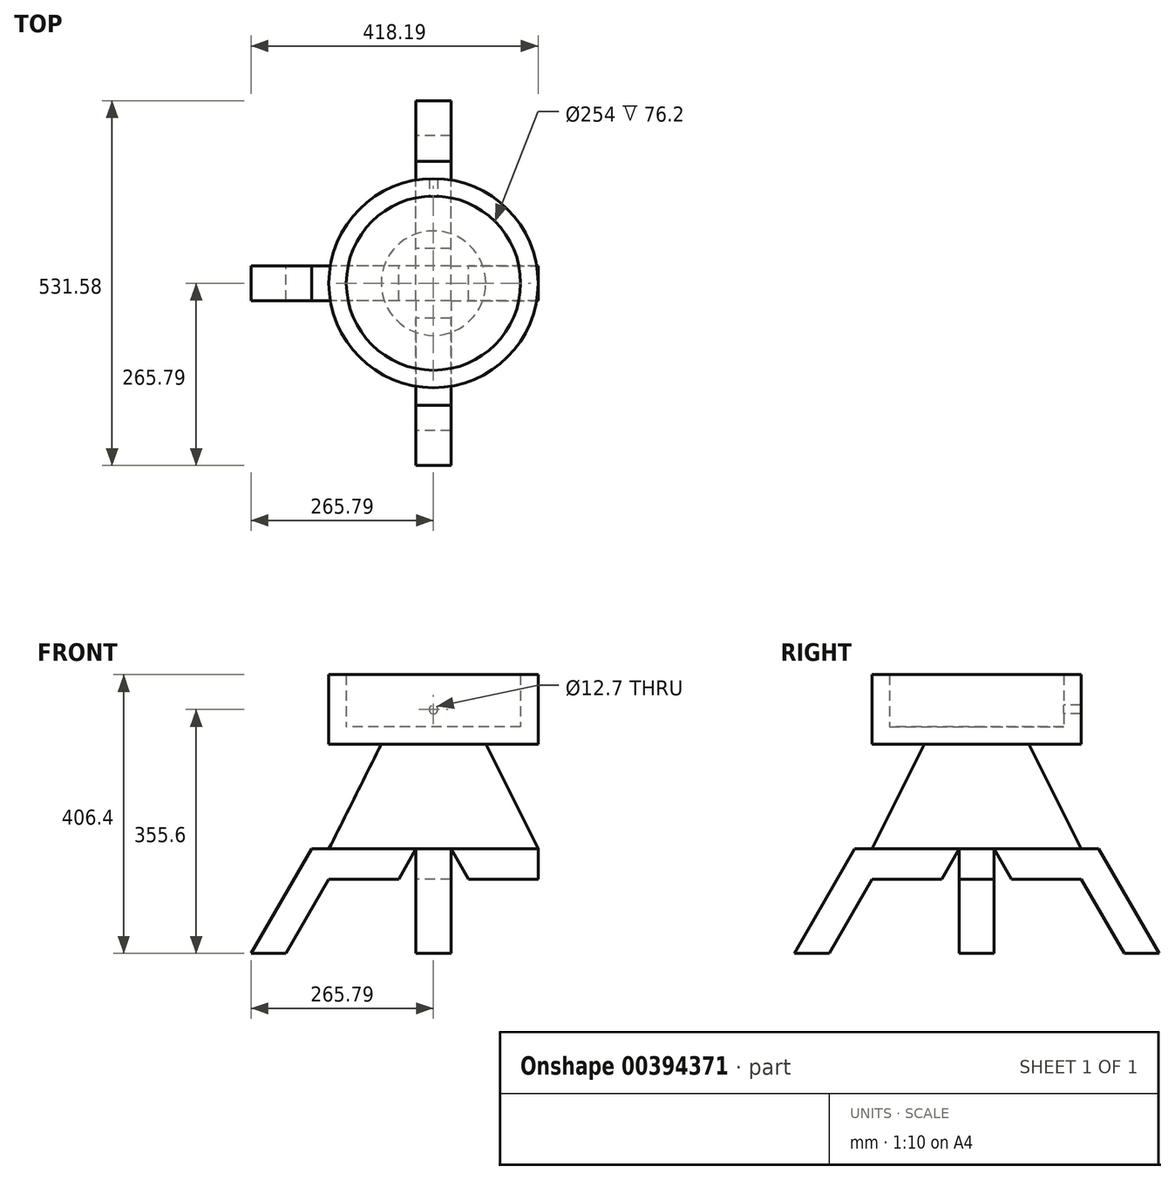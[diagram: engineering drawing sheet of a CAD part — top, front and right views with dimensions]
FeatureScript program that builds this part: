
annotation { "Feature Type Name" : "Feature", "Feature Type Description" : "" }
export const myFeature = defineFeature(function(context is Context, id is Id, definition is map)
    precondition{}
    {
        {
            var Q0;
            Q0=qCreatedBy(makeId("Top.planeOp"),FACE);
            var sketch = newSketch(context, id + "F0", { "sketchPlane" : qUnion([Q0])});
            skCircle(sketch, "E0", {"center": v(0, 0) * mm, "radius": 152.4 * mm});
            skCircle(sketch, "E1", {"center": v(0, 0) * mm, "radius": 127 * mm});
            skSolve(sketch);
        }
        {
            var Q0;
            Q0=makeQuery(id+"F0.imprint","IMPRINT",FACE,{"disambiguationData":[TD([[makeQuery(id+"F0.imprint","IMPRINT",EDGE,{"derivedFrom":sQuery(id+"F0.wireOp",EDGE,"E1")}),1.0]])]});
            extrude(context, id + "F1", {"entities" : qUnion([Q0]), "depth" : 25.4 * mm});
        }
        {
            var Q0;
            Q0 = qSketchRegion(id + "F0", true);
            extrude(context, id + "F2", {"entities" : qUnion([Q0]), "operationType" : NewBodyOperationType.ADD, "depth" : 101.6 * mm});
        }
        {
            var Q0;
            Q0=qCreatedBy(makeId("Front.planeOp"),FACE);
            var sketch = newSketch(context, id + "F3", { "sketchPlane" : qUnion([Q0])});
            skCircle(sketch, "E2", {"center": v(0, 50.8) * mm, "radius": 6.35 * mm});
            skSolve(sketch);
        }
        {
            var Q0;
            Q0 = qSketchRegion(id + "F3", true);
            extrude(context, id + "F4", {"entities" : qUnion([Q0]), "operationType" : NewBodyOperationType.REMOVE, "endBound" : BoundingType.THROUGH_ALL, "oppositeDirection" : true, "depth" : 25.4 * mm});
        }
        {
            var Q0;
            {var subQ0=sQuery(id+"F0.wireOp",EDGE,"E1");Q0=makeQuery(id+"F2.boolean.opBoolean","MERGE",FACE,{"derivedFrom":[makeQuery(id+"F1.opExtrude","CAP_FACE",FACE,{"disambiguationData":[OSD([subQ0])],"isStart":true}),makeQuery(id+"F2.opExtrude","CAP_FACE",FACE,{"disambiguationData":[OSD([sQuery(id+"F0.wireOp",EDGE,"E0"),subQ0])],"isStart":true})]});}
            var sketch = newSketch(context, id + "F5", { "sketchPlane" : qUnion([Q0])});
            skCircle(sketch, "E3", {"center": v(0, 0) * mm, "radius": 76.2 * mm});
            skSolve(sketch);
        }
        {
            var Q0;
            Q0=makeQuery(id+"F5.imprint","IMPRINT",FACE,{"disambiguationData":[TD([[makeQuery(id+"F5.imprint","IMPRINT",EDGE,{"derivedFrom":sQuery(id+"F5.wireOp",EDGE,"E3")}),-1.0]])]});
            cPlane(context, id + "F6", {"entities" : qUnion([Q0]), "cplaneType" : CPlaneType.OFFSET, "offset" : 152.4 * mm, "width" : 152.4 * mm, "height" : 152.4 * mm});
        }
        {
            var Q0;
            Q0=qCreatedBy(id+"F6.planeOp",FACE);
            var sketch = newSketch(context, id + "F7", { "sketchPlane" : qUnion([Q0])});
            skCircle(sketch, "E4", {"center": v(0, 0) * mm, "radius": 152.4 * mm});
            skSolve(sketch);
        }
        {
            var Q1;
            Q1 = qSketchRegion(id + "F5", true);
            var Q2;
            Q2 = qSketchRegion(id + "F7", true);
            loft(context, id + "F8", {"operationType" : NewBodyOperationType.ADD, "sheetProfilesArray" : [{ "sheetProfileEntities" : qUnion([Q1]) }, { "sheetProfileEntities" : qUnion([Q2]) }]});
        }
        {
            var Q0;
            Q0=qCreatedBy(makeId("Front.planeOp"),FACE);
            var sketch = newSketch(context, id + "F9", { "sketchPlane" : qUnion([Q0])});
            skLineSegment(sketch, "E5", {"start": v(-25.4, -152.4) * mm, "end": v(-177.8, -152.4) * mm});
            skPoint(sketch, "E6", {"position": v(0, -152.4) * mm});
            skLineSegment(sketch, "E7", {"start": v(-25.4, -152.4) * mm, "end": v(-152.4, -152.4) * mm});
            skLineSegment(sketch, "E8", {"start": v(-25.4, -152.4) * mm, "end": v(-50.8, -196.4) * mm});
            skLineSegment(sketch, "E9", {"start": v(-50.8, -196.4) * mm, "end": v(-152.4, -196.4) * mm});
            skLineSegment(sketch, "E10", {"start": v(-152.4, -304.8) * mm, "end": v(-385.64, -304.8) * mm});
            skLineSegment(sketch, "E11", {"start": v(-177.8, -152.4) * mm, "end": v(-265.79, -304.8) * mm});
            skLineSegment(sketch, "E12", {"start": v(-152.4, -196.4) * mm, "end": v(-214.99, -304.8) * mm});
            skLineSegment(sketch, "E13", {"start": v(0, -152.4) * mm, "end": v(0, -335.7) * mm});
            skLineSegment(sketch, "E14", {"start": v(25.4, -152.4) * mm, "end": v(177.8, -152.4) * mm});
            skLineSegment(sketch, "E15", {"start": v(25.4, -152.4) * mm, "end": v(50.8, -196.4) * mm});
            skLineSegment(sketch, "E16", {"start": v(177.8, -152.4) * mm, "end": v(152.4, -152.4) * mm});
            skLineSegment(sketch, "E17", {"start": v(152.4, -152.4) * mm, "end": v(152.4, -196.4) * mm});
            skLineSegment(sketch, "E18", {"start": v(152.4, -196.4) * mm, "end": v(50.8, -196.4) * mm});
            skPoint(sketch, "E19.endSnap0", {"position": v(152.4, -174.4) * mm});
            skLineSegment(sketch, "E20", {"start": v(177.8, -152.4) * mm, "end": v(265.79, -304.8) * mm});
            skLineSegment(sketch, "E21", {"start": v(265.79, -304.8) * mm, "end": v(214.99, -304.8) * mm});
            skLineSegment(sketch, "E22", {"start": v(152.4, -196.4) * mm, "end": v(214.99, -304.8) * mm});
            skSolve(sketch);
        }
        {
            var Q0;
            Q0=makeQuery(id+"F9.imprint","IMPRINT",FACE,{"disambiguationData":[TD([[makeQuery(id+"F9.imprint","IMPRINT",EDGE,{"derivedFrom":sQuery(id+"F9.wireOp",EDGE,"E5")}),1.0]])]});
            var Q1;
            Q1=makeQuery(id+"F9.imprint","IMPRINT",FACE,{"disambiguationData":[TD([[makeQuery(id+"F9.imprint","IMPRINT",EDGE,{"derivedFrom":sQuery(id+"F9.wireOp",EDGE,"E16")}),1.0]])]});
            var Q2;
            Q2=makeQuery(id+"F9.imprint","IMPRINT",FACE,{"disambiguationData":[TD([[makeQuery(id+"F9.imprint","IMPRINT",EDGE,{"derivedFrom":sQuery(id+"F9.wireOp",EDGE,"E14")}),-1.0]])]});
            extrude(context, id + "F10", {"entities" : qUnion([Q0, Q1, Q2]), "operationType" : NewBodyOperationType.ADD, "endBound" : BoundingType.SYMMETRIC, "depth" : 50.8 * mm});
        }
        {
            var Q0;
            Q0=qCreatedBy(makeId("Right.planeOp"),FACE);
            var sketch = newSketch(context, id + "F11", { "sketchPlane" : qUnion([Q0])});
            skLineSegment(sketch, "E23", {"start": v(0, 0) * mm, "end": v(0, -152.4) * mm});
            skLineSegment(sketch, "E24", {"start": v(0, -152.4) * mm, "end": v(0, 0) * mm});
            skLineSegment(sketch, "E25", {"start": v(0, -152.4) * mm, "end": v(25.4, -152.4) * mm});
            skLineSegment(sketch, "E26", {"start": v(25.4, -152.4) * mm, "end": v(177.8, -152.4) * mm});
            skLineSegment(sketch, "E27", {"start": v(25.4, -152.4) * mm, "end": v(25.4, -196.4) * mm});
            skLineSegment(sketch, "E28", {"start": v(25.4, -152.4) * mm, "end": v(50.8, -196.4) * mm});
            skLineSegment(sketch, "E29", {"start": v(25.4, -152.4) * mm, "end": v(152.4, -152.4) * mm});
            skLineSegment(sketch, "E30", {"start": v(152.4, -152.4) * mm, "end": v(152.4, -304.8) * mm});
            skLineSegment(sketch, "E31", {"start": v(177.8, -152.4) * mm, "end": v(265.79, -304.8) * mm});
            skLineSegment(sketch, "E32", {"start": v(152.4, -196.4) * mm, "end": v(214.99, -304.8) * mm});
            skLineSegment(sketch, "E33", {"start": v(214.99, -304.8) * mm, "end": v(265.79, -304.8) * mm});
            skLineSegment(sketch, "E34", {"start": v(50.8, -196.4) * mm, "end": v(152.4, -196.4) * mm});
            skLineSegment(sketch, "E35", {"start": v(0, -152.4) * mm, "end": v(-25.4, -152.4) * mm});
            skLineSegment(sketch, "E36", {"start": v(-25.4, -152.4) * mm, "end": v(-25.4, -196.4) * mm});
            skLineSegment(sketch, "E37", {"start": v(-25.4, -152.4) * mm, "end": v(-177.8, -152.4) * mm});
            skLineSegment(sketch, "E38", {"start": v(-25.4, -152.4) * mm, "end": v(-50.8, -196.4) * mm});
            skLineSegment(sketch, "E39", {"start": v(-177.8, -152.4) * mm, "end": v(-152.4, -152.4) * mm});
            skLineSegment(sketch, "E40", {"start": v(-265.79, -304.8) * mm, "end": v(-177.8, -152.4) * mm});
            skLineSegment(sketch, "E41", {"start": v(-152.4, -196.4) * mm, "end": v(-214.99, -304.8) * mm});
            skLineSegment(sketch, "E42", {"start": v(-265.79, -304.8) * mm, "end": v(-214.99, -304.8) * mm});
            skLineSegment(sketch, "E43", {"start": v(-152.4, -152.4) * mm, "end": v(-152.4, -196.4) * mm});
            skLineSegment(sketch, "E44", {"start": v(-152.4, -196.4) * mm, "end": v(-50.8, -196.4) * mm});
            skSolve(sketch);
        }
        {
            var Q0;
            Q0 = qSketchRegion(id + "F11", true);
            extrude(context, id + "F12", {"entities" : qUnion([Q0]), "operationType" : NewBodyOperationType.ADD, "endBound" : BoundingType.SYMMETRIC, "depth" : 50.8 * mm});
        }
    });
